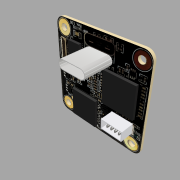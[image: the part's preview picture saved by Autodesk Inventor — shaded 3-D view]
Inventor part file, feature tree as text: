
AUTODESK INVENTOR PART (.ipt)
format: ipt  version: 2019 (Build 230136000, 136)  size: 8,272,896 bytes
history: native  units: mm
features: sketch x13, other x12, extrude x11, projected_geometry x2, plane x1, chamfer x1
ambient origin geometry x8: Origin, YZ Plane, XZ Plane, XY Plane, X Axis, Y Axis, Z Axis, Center Point
bodies: Body1 (feature_tree), Body2 (feature_tree), Body3 (feature_tree), Body4 (feature_tree), Body5 (feature_tree), Body6 (feature_tree), Body7 (feature_tree)
feature tree (40):
  other  "PCB"
  extrude  "PCB Extrusion"  Depth=30.0mm
  other  "Decal1"
  other  "Decal2"
  extrude  "Chip Carrier A"  Depth=2.5mm
  extrude  "Chip Carrier B"  Depth=2.1mm
  extrude  "Chip Carrier C"  Depth=24.5mm
  extrude  "Chip Carrier D"  Depth=24.5mm
  extrude  "Chip Carrier E"  TaperAngle=0.0deg  [1 undecoded]
  plane  "Work Plane1"
  extrude  "Chip Carriet F"  Depth=12.25mm
  extrude  "USB_C Extrusion"  Depth=1.0mm TaperAngle=0.0deg
  extrude  "JST_Body Extrusion"  Depth=12.5mm
  sketch  "Sketch13"  dims[d27=6.75mm d28=3.2mm d29=5.13mm d30=5.62mm d31=0.25mm d32=4.2mm d33=0.0mm d34=0.2mm d35=0.5mm d36=0.0mm d37=1.5mm d38=1.0mm d39=0.96mm d40=0.0mm d41=11.0mm d42=8.0mm d43=0.85mm d44=0.0mm d45=7.7976mm d46=4.332mm d47=0.05mm d48=0.0mm d49=0.45mm d50=0.0mm d51=0.05mm d52=10.0mm d53=10.0mm d54=1.75mm d55=2.75mm d56=9.0mm d57=9.0mm d58=0.0mm d59=1.0mm d60=4.5mm d61=4.0mm d62=3.0mm d63=0.75mm d64=4.0mm d65=4.0mm d67=3.0mm d68=1.0mm d69=0.0mm d88=1.269452mm d89=3.5mm d90=0.0mm d91=0.2mm d92=2.0mm d93=45.0deg d94=1.8mm]
  extrude  "JST_Pins Extrusion"  Depth=1.96mm
  extrude  "Back ICs Extrusion"  TaperAngle=0.0deg  [1 undecoded]
  chamfer  "Chamfer1"  Distance=8.8mm
  other  "Mask_Plane_1.8mm"
  sketch  "Sketch1"  dims[d0=30.0mm d1=30.0mm]
  sketch  "Sketch2"  dims[d2=2.5mm d3=2.1mm]
  other  "Chip Carrier"
  sketch  "Sketch3"  dims[d4=2.1mm d5=2.1mm]
  other  "USB_C"
  sketch  "Sketch4"  dims[d6=2.1mm d7=24.5mm]
  other  "JST Body"
  sketch  "Sketch5"  dims[d8=24.5mm d9=24.5mm]
  projected_geometry  "Projected Loop1"
  sketch  "Sketch6"  dims[d10=24.5mm d11=0.0mm]
  projected_geometry  "Projected Loop2"
  sketch  "Sketch7"  dims[d12=0.0mm d13=12.25mm]
  sketch  "Sketch8"  dims[d14=12.25mm d15=1.0mm d16=0.0mm]
  sketch  "Sketch9"  dims[d17=15.0mm d18=12.5mm]
  other  "Chip Carrier Coverglass"
  sketch  "Sketch10"  dims[d19=1.96mm d20=0.0mm d21=8.74mm]
  other  "Back ICs"
  sketch  "Sketch11"  dims[d22=2.96mm d23=0.0mm]
  other  "Image1"
  sketch  "Sketch12"  dims[d24=8.52mm d25=8.8mm d26=0.0mm]
  other  "Image2"
  other  "JST Pins"
note: 2 required parameter values undecoded (feature->parameter linkage not recoverable at this tier; creation-order binding heuristic only, values carry confidence <= 0.55)
